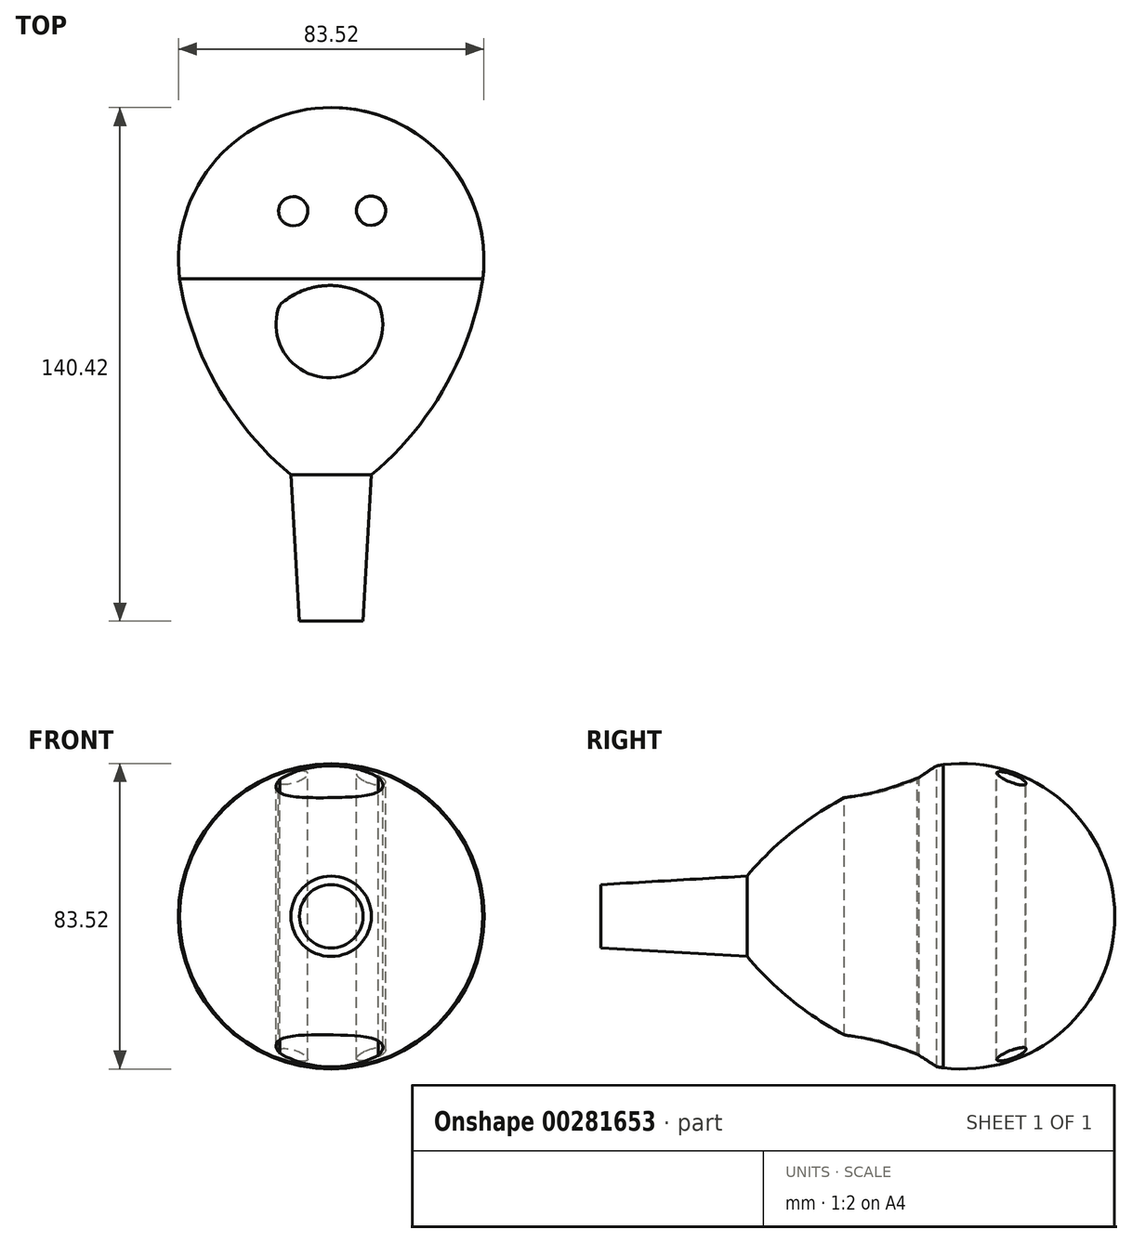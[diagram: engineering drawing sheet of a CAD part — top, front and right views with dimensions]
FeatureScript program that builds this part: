
annotation { "Feature Type Name" : "Feature", "Feature Type Description" : "" }
export const myFeature = defineFeature(function(context is Context, id is Id, definition is map)
    precondition{}
    {
        {
            var Q0;
            Q0=qCreatedBy(makeId("Top.planeOp"),FACE);
            var sketch = newSketch(context, id + "F0", { "sketchPlane" : qUnion([Q0])});
            skLineSegment(sketch, "E0", {"start": v(0, 0) * mm, "end": v(-11, 0) * mm});
            skLineSegment(sketch, "E1", {"start": v(-11, 0) * mm, "end": v(-8.67, -39.93) * mm});
            skLineSegment(sketch, "E2", {"start": v(-8.67, -39.93) * mm, "end": v(0, -39.93) * mm});
            skLineSegment(sketch, "E3", {"start": v(0, -39.93) * mm, "end": v(0, 0) * mm});
            skLineSegment(sketch, "E4", {"start": v(0, 100.49) * mm, "end": v(0, 100.49) * mm});
            skLineSegment(sketch, "E5", {"start": v(0, 100.49) * mm, "end": v(0, 0) * mm});
            skArc(sketch, "E6", {"start": v(-41.45, 53.6) * mm, "mid": v(-31.05, 24.06) * mm, "end": v(-11, 0) * mm});
            skArc(sketch, "E7", {"start": v(0, 100.49) * mm, "mid": v(-31.29, 86.39) * mm, "end": v(-41.45, 53.6) * mm});
            skSolve(sketch);
        }
        {
            var Q0;
            Q0 = qSketchRegion(id + "F0", true);
            var Q1;
            Q1=sQuery(id+"F0.wireOp",EDGE,"E5");
            revolve(context, id + "F1", {"entities" : qUnion([Q0]), "axis" : qUnion([Q1]), "revolveType" : RevolveType.FULL});
        }
        {
            var Q0;
            Q0=qCreatedBy(makeId("Top.planeOp"),FACE);
            var sketch = newSketch(context, id + "F2", { "sketchPlane" : qUnion([Q0])});
            skCircle(sketch, "E8", {"center": v(10.9, 72.27) * mm, "radius": 4 * mm});
            skCircle(sketch, "E9", {"center": v(-10.38, 72.14) * mm, "radius": 4 * mm});
            skArc(sketch, "E10", {"start": v(-14.11, 46.46) * mm, "mid": v(-0.22, 26.6) * mm, "end": v(12.93, 46.95) * mm});
            skArc(sketch, "E11", {"start": v(12.93, 46.95) * mm, "mid": v(-0.68, 51.82) * mm, "end": v(-14.11, 46.46) * mm});
            skSolve(sketch);
        }
        {
            var Q0;
            Q0 = qSketchRegion(id + "F2", true);
            extrude(context, id + "F3", {"entities" : qUnion([Q0]), "operationType" : NewBodyOperationType.REMOVE, "endBound" : BoundingType.THROUGH_ALL, "oppositeDirection" : true, "depth" : 25 * mm});
        }
        {
            var Q0;
            Q0 = qSketchRegion(id + "F2", true);
            extrude(context, id + "F4", {"entities" : qUnion([Q0]), "operationType" : NewBodyOperationType.REMOVE, "endBound" : BoundingType.THROUGH_ALL, "depth" : 25 * mm});
        }
    });
